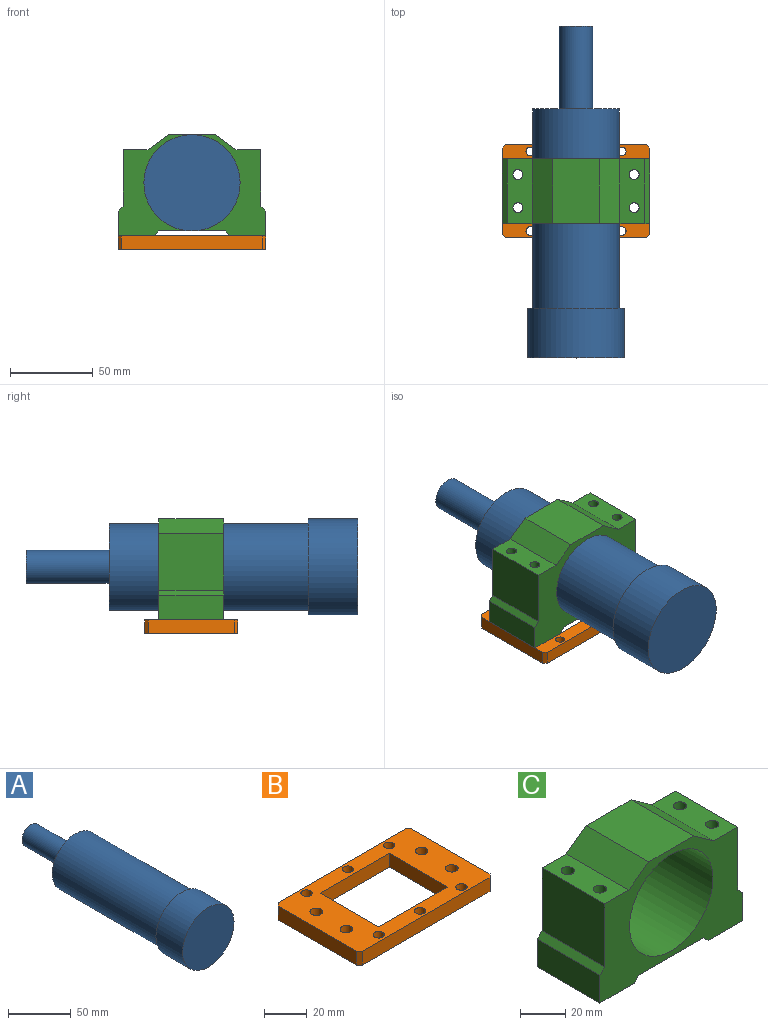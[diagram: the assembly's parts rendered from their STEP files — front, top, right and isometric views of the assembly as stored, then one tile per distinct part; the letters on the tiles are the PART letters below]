
ASSEMBLY  parts=3 mates=2
PART A: 7 faces, bbox 58x200x58 mm
  f0: cylinder r=26mm len=120mm, axis (0,1,0), area 19603.5mm2, adj f1,f4
  f1: plane 52x52mm, normal (0,1,0), area 1809.6mm2, adj f0,f5
  f2: cylinder r=29mm len=58mm, axis (0,1,0), area 5466.4mm2, adj f3,f4
  f3: plane 58x58mm, normal (0,-1,0), area 2642.1mm2, adj f2
  f4: plane 58x58mm, normal (0,1,0), area 518.4mm2, adj f0,f2
  f5: cylinder r=10mm len=50mm, axis (0,-1,0), area 3141.6mm2, adj f1,f6
  f6: plane 20x20mm, normal (0,1,0), area 314.2mm2, adj f5
PART B: 24 faces, bbox 89x56x8 mm
  f0: plane 85x8mm, normal (0,1,0), area 680mm2, adj f18,f19,f20,f21
  f1: plane 52x8mm, normal (1,0,0), area 416mm2, adj f18,f19,f21,f23
  f2: plane 85x8mm, normal (0,-1,0), area 680mm2, adj f18,f19,f22,f23
  f3: plane 46x8mm, normal (0,1,0), area 368mm2, adj f4,f16,f18,f19
  f4: plane 39x8mm, normal (-1,0,0), area 312mm2, adj f3,f5,f18,f19
  f5: plane 46x8mm, normal (0,-1,0), area 368mm2, adj f4,f16,f18,f19
  f6: cylinder r=3mm len=8mm, axis (0,0,1), area 150.8mm2, adj f18,f19
  f7: cylinder r=3mm len=8mm, axis (0,0,1), area 150.8mm2, adj f18,f19
  f8: cylinder r=3mm len=8mm, axis (0,0,1), area 150.8mm2, adj f18,f19
  f9: cylinder r=3mm len=8mm, axis (0,0,1), area 150.8mm2, adj f18,f19
  f10: cylinder r=2.65mm len=8mm, axis (0,0,1), area 133.2mm2, adj f18,f19
  f11: cylinder r=2.65mm len=8mm, axis (0,0,1), area 133.2mm2, adj f18,f19
  f12: cylinder r=2.65mm len=8mm, axis (0,0,1), area 133.2mm2, adj f18,f19
  f13: cylinder r=2.65mm len=8mm, axis (0,0,1), area 133.2mm2, adj f18,f19
  f14: cylinder r=2.65mm len=8mm, axis (0,0,1), area 133.2mm2, adj f18,f19
  f15: cylinder r=2.65mm len=8mm, axis (0,0,1), area 133.2mm2, adj f18,f19
  f16: plane 39x8mm, normal (1,0,0), area 312mm2, adj f3,f5,f18,f19
  f17: plane 52x8mm, normal (-1,0,0), area 416mm2, adj f18,f19,f20,f22
  f18: plane 89x56mm, normal (0,0,-1), area 2936.5mm2, adj f0,f1,f2,f3,f4,f5,f6,f7
  f19: plane 89x56mm, normal (0,0,1), area 2936.5mm2, adj f0,f1,f2,f3,f4,f5,f6,f7
  f20: plane 8x2mm, normal (-0.71,0.71,0), area 22.6mm2, adj f0,f17,f18,f19
  f21: plane 8x2mm, normal (0.71,0.71,0), area 22.6mm2, adj f0,f1,f18,f19
  f22: plane 8x2mm, normal (-0.71,-0.71,0), area 22.6mm2, adj f2,f17,f18,f19
  f23: plane 8x2mm, normal (0.71,-0.71,0), area 22.6mm2, adj f1,f2,f18,f19
PART C: 23 faces, bbox 89x39x61 mm
  f0: plane 39x21.5mm, normal (0,0,-1), area 782mm2, adj f4,f5,f17,f18,f19,f20
  f1: plane 39x21.5mm, normal (0,0,-1), area 782mm2, adj f7,f8,f17,f18,f21,f22
  f2: plane 39x15mm, normal (0,0,1), area 528.5mm2, adj f10,f11,f17,f18,f21,f22
  f3: plane 39x15mm, normal (0,0,1), area 528.5mm2, adj f13,f14,f17,f18,f19,f20
  f4: plane 39x15mm, normal (-1,0,0), area 585mm2, adj f0,f16,f17,f18
  f5: plane 39x3mm, normal (0.71,0,-0.71), area 165.5mm2, adj f0,f6,f17,f18
  f6: plane 40x39mm, normal (0,0,-1), area 1560mm2, adj f5,f7,f17,f18
  f7: plane 39x3mm, normal (-0.71,0,-0.71), area 165.5mm2, adj f1,f6,f17,f18
  f8: plane 39x15mm, normal (1,0,0), area 585mm2, adj f1,f9,f17,f18
  f9: plane 39x3mm, normal (0.71,0,0.71), area 165.5mm2, adj f8,f10,f17,f18
  f10: plane 39x34mm, normal (1,0,0), area 1326mm2, adj f2,f9,f17,f18
  f11: plane 39x12.5mm, normal (0.58,0,0.81), area 600.7mm2, adj f2,f12,f17,f18
  f12: plane 39x28mm, normal (0,0,1), area 1092mm2, adj f11,f13,f17,f18
  f13: plane 39x12.5mm, normal (-0.58,0,0.81), area 600.7mm2, adj f3,f12,f17,f18
  f14: plane 39x34mm, normal (-1,0,0), area 1326mm2, adj f3,f16,f17,f18
  f15: cylinder r=26mm len=52mm, axis (0,1,0), area 6371.1mm2, adj f17,f18
  f16: plane 39x3mm, normal (-0.71,0,0.71), area 165.5mm2, adj f4,f14,f17,f18
  f17: plane 89x61mm, normal (0,-1,0), area 2526.8mm2, adj f0,f1,f2,f3,f4,f5,f6,f7
  f18: plane 89x61mm, normal (0,1,0), area 2526.8mm2, adj f0,f1,f2,f3,f4,f5,f6,f7
  f19: cylinder r=3mm len=52mm, axis (0,0,1), area 980.2mm2, adj f0,f3
  f20: cylinder r=3mm len=52mm, axis (0,0,1), area 980.2mm2, adj f0,f3
  f21: cylinder r=3mm len=52mm, axis (0,0,1), area 980.2mm2, adj f1,f2
  f22: cylinder r=3mm len=52mm, axis (0,0,1), area 980.2mm2, adj f1,f2
PLACE A t=(-25.48,93.62,-7.83)mm
PLACE B t=(-25.48,-0.38,17.17)mm
PLACE C t=(-25.48,-0.38,-7.83)mm fixed
MATE fastened C.f15 <-> A.f0  axis (0,1,0) through (-20.27,-0.38,-10.76)mm
MATE fastened C.f20 <-> B.f6  axis (0,0,-1) through (-55.27,-29.88,-42.76)mm
